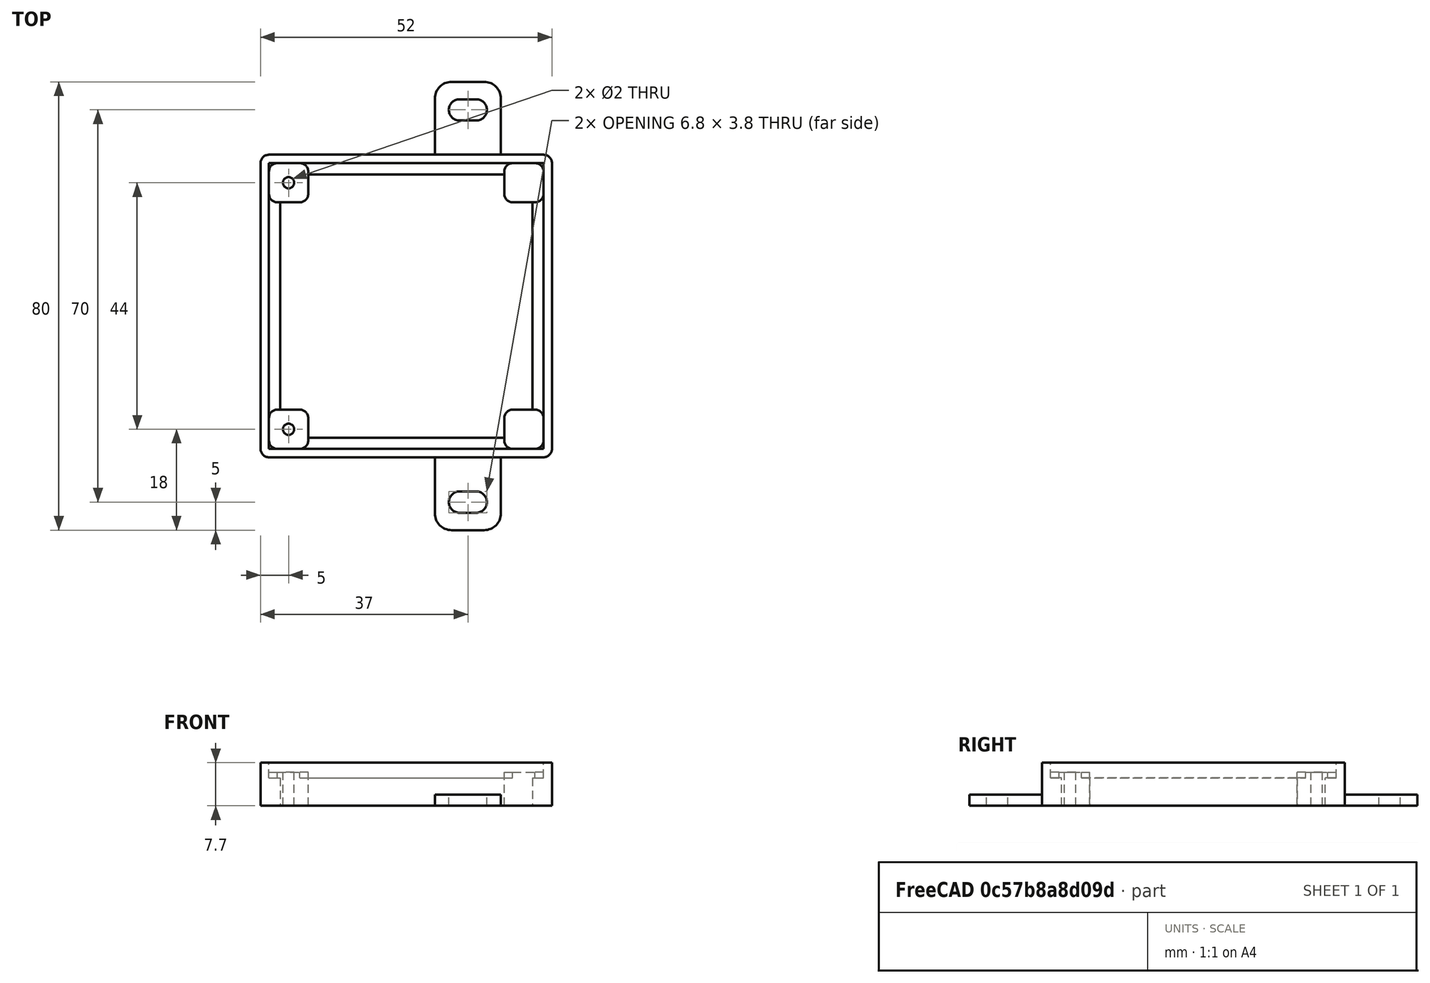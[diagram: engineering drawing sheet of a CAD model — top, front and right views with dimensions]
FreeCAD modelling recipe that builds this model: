
FCSTD DOCUMENT  (FreeCAD 0.19R)
Label: pcb_7x5_cut
License: All rights reserved
LicenseURL: http://en.wikipedia.org/wiki/All_rights_reserved
objects: Part::Box×4, Part::MultiFuse×3, Part::FeaturePython×2, Part::Fillet×2, Part::Cut×2, Part::Cylinder×1, Spreadsheet::Sheet×1, Part::Feature×1, App::Part×1
note: 15 computed .brp shape members not serialized (recipe doc carries the construction recipe); baked Part::Feature solids carry a one-line shape summary decoded from their .brp

FEATURE [Part::Cylinder] Cylinder  label="pcb hole"
  Angle = 360
  AttacherType = Attacher::AttachEngine3D
  Height = 10
  Placement = pos=(5,5,0) rot=(0,0,1;0rad)
  Radius = 1
  expr: Radius = <<p>>.hole_r
  expr: .Placement.Base.y = (<<p>>.box_wall * 2 + <<p>>.pcb_y - <<p>>.hole_y_dist) / 2
FEATURE [Part::FeaturePython] Array001  label="hole array"  # Draft array (typed FeaturePython)
  Angle = 360
  ArrayType = 0
  Axis = (0,0,1)
  Base = -> Cylinder
  Center = (0,0,0)
  Fuse = false
  IntervalAxis = (0,0,0)
  IntervalX = (64,0,0)
  IntervalY = (0,44,0)
  IntervalZ = (0,0,1)
  NumberPolar = 1
  NumberX = 2
  NumberY = 2
  NumberZ = 1
  expr: .IntervalX.x = <<p>>.hole_x_dist
  expr: .IntervalY.y = <<p>>.hole_y_dist
FEATURE [Part::Box] Box  label="bottom cube"
  AttacherType = Attacher::AttachEngine3D
  Height = 7.7
  Length = 52
  Width = 54
  expr: Height = <<p>>.pcb_under + <<p>>.pcb_height + <<p>>.under_layer
  expr: Length = <<p>>.pcb_x + <<p>>.box_wall * 2
  expr: Width = <<p>>.pcb_y + <<p>>.box_wall * 2
FEATURE [Part::Fillet] Fillet001  label="bottom cube fillet"
  Base = -> Box
  Edges = 4 edges r=1.5: [Edge1,Edge3,Edge5,Edge7]
FEATURE [Spreadsheet::Sheet] Spreadsheet  label="p"
  cells = A1=hole_x_dist; B1(hole_x_dist)=64; A2=hole_y_dist; B2(hole_y_dist)=44; A3=dd_hole_x_dist; B3(dd_hole_x_dist)=66; A4=dd_hole_y_dist; B4(dd_hole_y_dist)=46; A5=pcb_under; B5(pcb_under)=3; A6=pcb_x; B6(pcb_x)=49; A7=pcb_cut_x; B7(pcb_cut_x)=49; A8=pcb_y; B8(pcb_y)=51; A9=hole_stand_x; B9(hole_stand_x)=7; A10=hole_stand_y; B10(hole_stand_y)=7; A11=hole_r; B11(hole_r)=1; A12=box_wall; B12(box_wall)=1.5; A13=under_layer; B13(under_layer)=3; A14=pcb_height; B14(pcb_height)=1.7; A15=under_pcb_border; B15(under_pcb_border)=2
FEATURE [Part::Feature] Cut002002  label="attach plane y dir002"
  Placement = pos=(31.1,-13,0) rot=(0,0,1;0rad)
  shape: bbox 11.8 x 80 x 2 mm, 20 faces (baked)
FEATURE [Part::Box] Box002  label="pcb extraction"
  AttacherType = Attacher::AttachEngine3D
  Height = 10
  Length = 49
  Placement = pos=(1.5,1.5,5) rot=(0,0,1;0rad)
  Width = 51
  expr: Width = <<p>>.pcb_y
  expr: Length = <<p>>.pcb_x
  expr: .Placement.Base.x = <<p>>.box_wall
  expr: .Placement.Base.y = <<p>>.box_wall
  expr: .Placement.Base.z = <<p>>.under_pcb_border + <<p>>.under_layer
FEATURE [Part::Box] Box003  label="hole stand cube"
  AttacherType = Attacher::AttachEngine3D
  Height = 6
  Length = 7
  Placement = pos=(1.5,1.5,0) rot=(0,0,1;0rad)
  Width = 7
  expr: Length = <<p>>.hole_stand_x
  expr: Width = <<p>>.hole_stand_y
  expr: Height = <<p>>.pcb_under + <<p>>.under_layer
  expr: .Placement.Base.x = <<p>>.box_wall
  expr: .Placement.Base.y = <<p>>.box_wall
FEATURE [Part::MultiFuse] Fusion002  label="bottom fusion"
  Shapes = -> [Fillet001,Cut002002]
FEATURE [Part::Box] Box001  label="bottom extraction"
  AttacherType = Attacher::AttachEngine3D
  Height = 10
  Length = 45
  Placement = pos=(3.5,3.5,0) rot=(0,0,1;0rad)
  Width = 47
  expr: Width = <<p>>.pcb_y - <<p>>.under_pcb_border * 2
  expr: Length = <<p>>.pcb_x - <<p>>.under_pcb_border * 2
  expr: .Placement.Base.x = <<p>>.under_pcb_border + <<p>>.box_wall
  expr: .Placement.Base.y = <<p>>.under_pcb_border + <<p>>.box_wall
FEATURE [Part::MultiFuse] Fusion  label="bottom extraction001"
  Shapes = -> [Box001,Box002]
FEATURE [Part::Cut] Cut  label="pcb box cut"
  Base = -> Fusion002
  Tool = -> Fusion
FEATURE [Part::Fillet] Fillet  label="stand fillet"
  Base = -> Box003
  Edges = 4 edges r=1.5: [Edge1,Edge3,Edge5,Edge7]
FEATURE [Part::FeaturePython] Array  label="hole stand array"  # Draft array (typed FeaturePython)
  Angle = 360
  ArrayType = 0
  Axis = (0,0,1)
  Base = -> Fillet
  Center = (0,0,0)
  Fuse = false
  IntervalAxis = (0,0,0)
  IntervalX = (42,0,0)
  IntervalY = (0,44,0)
  IntervalZ = (0,0,1)
  NumberPolar = 1
  NumberX = 2
  NumberY = 2
  NumberZ = 1
  expr: .IntervalX.x = <<p>>.pcb_x - <<p>>.hole_stand_x
  expr: .IntervalY.y = <<p>>.pcb_y - <<p>>.hole_stand_y
FEATURE [Part::MultiFuse] Fusion001  label="frame fusion"
  Shapes = -> [Array,Cut]
FEATURE [Part::Cut] Cut001  label="frame fusion with holes"
  Base = -> Fusion001
  Tool = -> Array001
FEATURE [App::Part] Part  label="special cut pcb with 4 holes siggle layer part"
  Group = -> [Fusion,Fusion002,Box002,Box001,Array001,Cut,Array,Cylinder,Fusion001,Cut001]
  Origin = -> Origin
